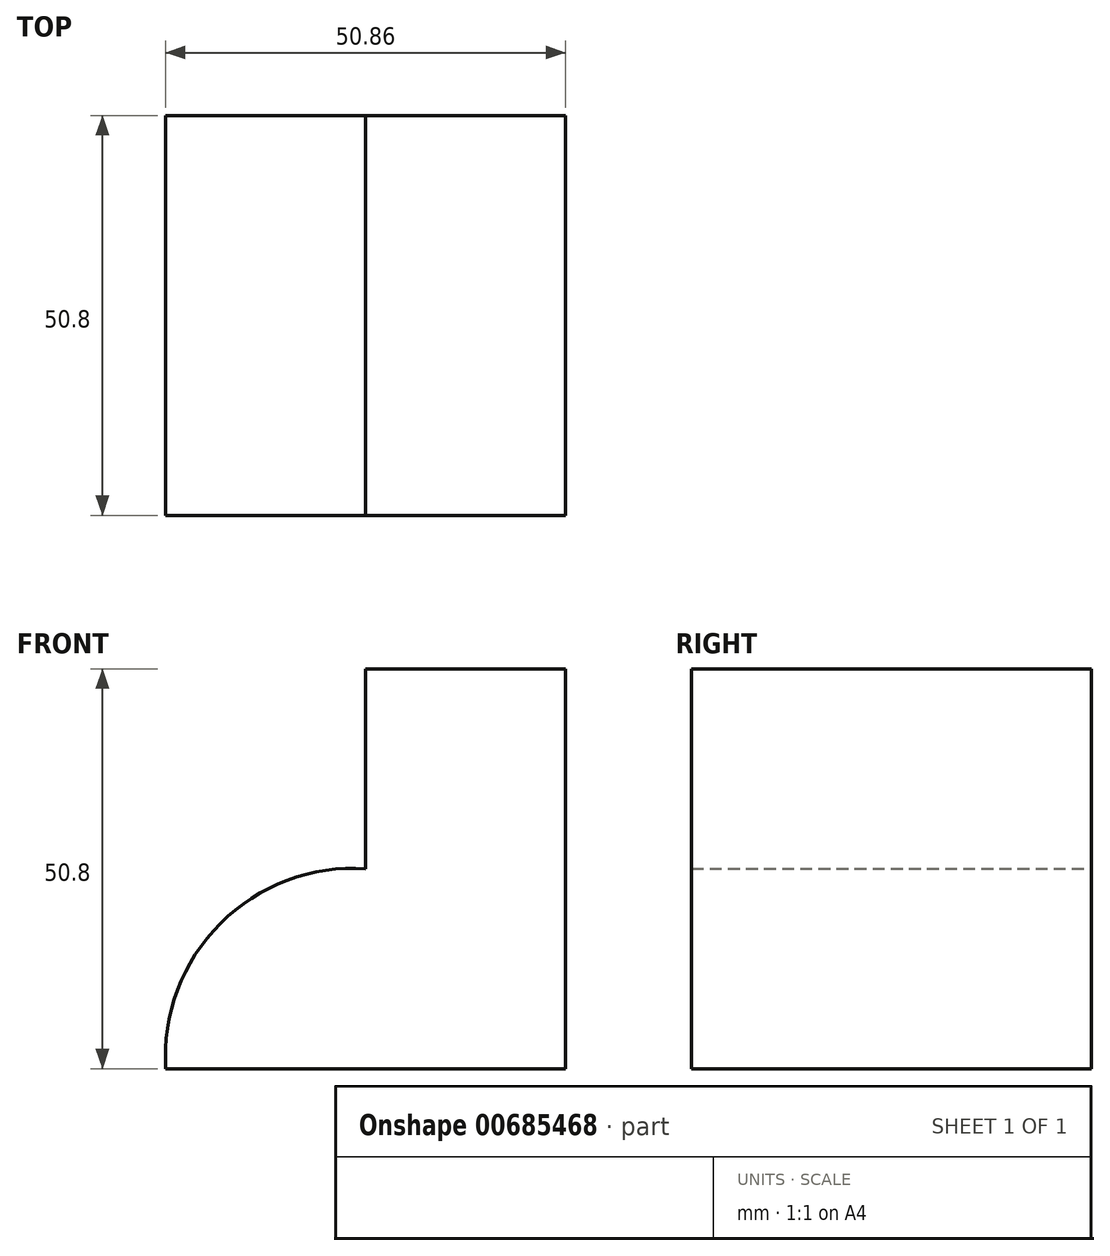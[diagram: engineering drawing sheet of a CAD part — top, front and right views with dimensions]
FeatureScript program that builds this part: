
annotation { "Feature Type Name" : "Feature", "Feature Type Description" : "" }
export const myFeature = defineFeature(function(context is Context, id is Id, definition is map)
    precondition{}
    {
        {
            var Q0;
            Q0=qCreatedBy(makeId("Front.planeOp"),FACE);
            var sketch = newSketch(context, id + "F0", { "sketchPlane" : qUnion([Q0])});
            skLineSegment(sketch, "E0", {"start": v(-28.35, 10.79) * mm, "end": v(-28.35, 36.19) * mm});
            skLineSegment(sketch, "E1", {"start": v(-28.35, 36.19) * mm, "end": v(-2.95, 36.19) * mm});
            skLineSegment(sketch, "E2", {"start": v(-2.95, 36.19) * mm, "end": v(-2.95, -14.61) * mm});
            skLineSegment(sketch, "E3", {"start": v(-2.95, -14.61) * mm, "end": v(-53.75, -14.61) * mm});
            skArc(sketch, "E4", {"start": v(-28.35, 10.79) * mm, "mid": v(-46.81, 3.85) * mm, "end": v(-53.75, -14.61) * mm});
            skSolve(sketch);
        }
        {
            var Q0;
            Q0=makeQuery(id+"F0.imprint","IMPRINT",FACE,{"disambiguationData":[TD([[makeQuery(id+"F0.imprint","IMPRINT",EDGE,{"derivedFrom":sQuery(id+"F0.wireOp",EDGE,"E0")}),-1.0]])]});
            extrude(context, id + "F1", {"entities" : qUnion([Q0]), "depth" : 50.8 * mm, "offsetDistance" : 25.4 * mm});
        }
    });
